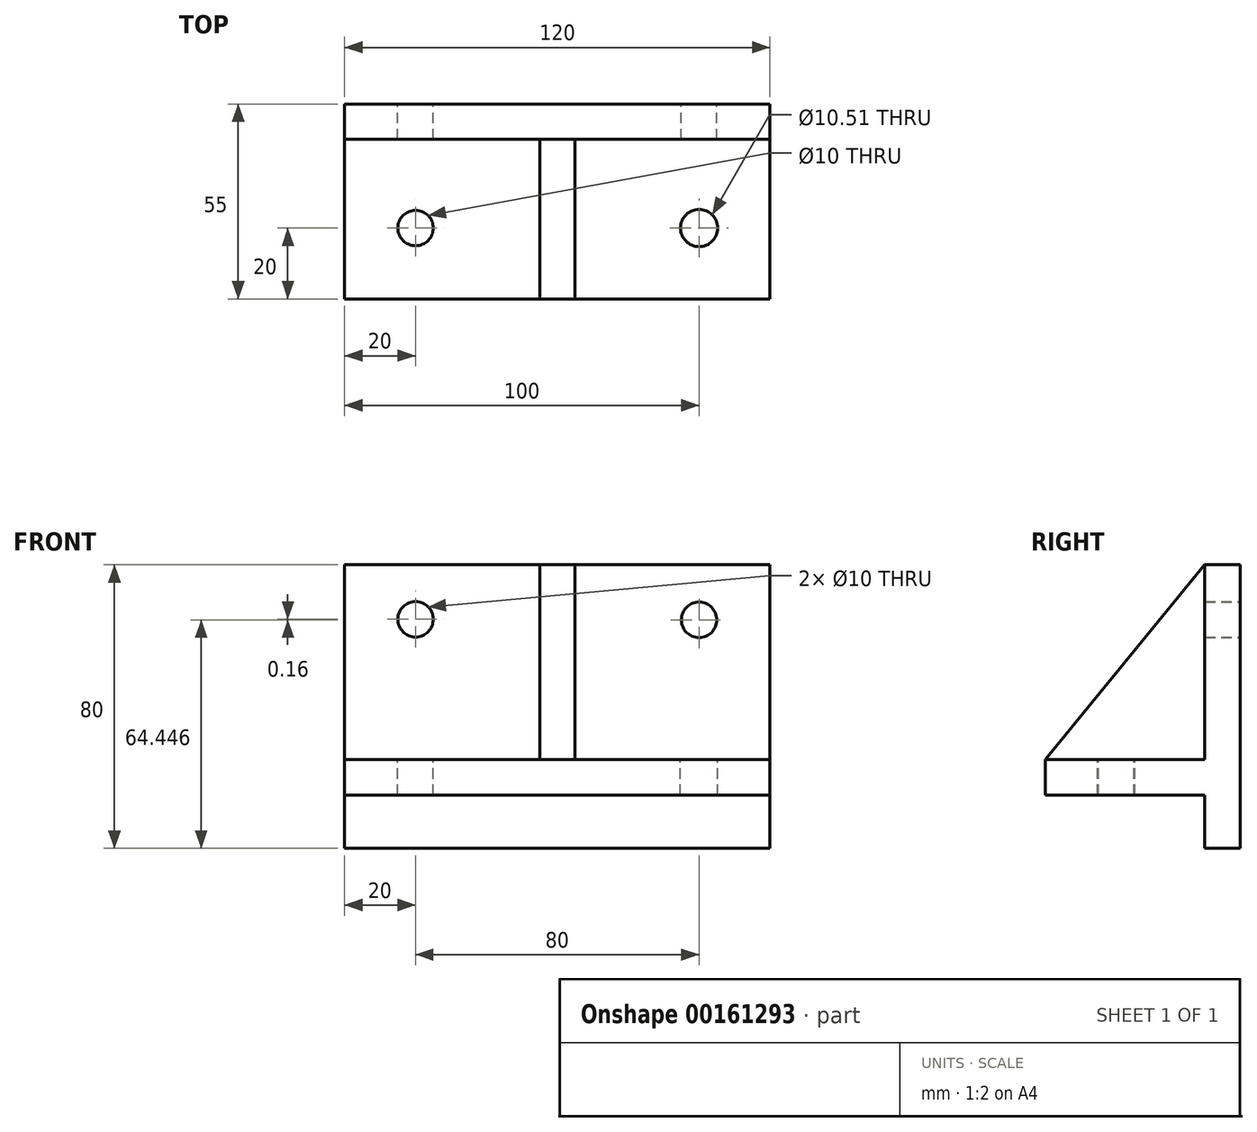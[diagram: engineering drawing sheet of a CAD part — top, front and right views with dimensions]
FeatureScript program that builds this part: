
annotation { "Feature Type Name" : "Feature", "Feature Type Description" : "" }
export const myFeature = defineFeature(function(context is Context, id is Id, definition is map)
    precondition{}
    {
        {
            var Q0;
            Q0=qCreatedBy(makeId("Front.planeOp"),FACE);
            var sketch = newSketch(context, id + "F0", { "sketchPlane" : qUnion([Q0])});
            skLineSegment(sketch, "E0.bottom", {"start": v(60, 40) * mm, "end": v(-60, 40) * mm});
            skLineSegment(sketch, "E0.top", {"start": v(60, -40) * mm, "end": v(-60, -40) * mm});
            skLineSegment(sketch, "E0.left", {"start": v(60, 40) * mm, "end": v(60, -40) * mm});
            skLineSegment(sketch, "E0.right", {"start": v(-60, 40) * mm, "end": v(-60, -40) * mm});
            skPoint(sketch, "E0.middle", {"position": v(0, 0) * mm});
            skCircle(sketch, "E1", {"center": v(-40, 24.6) * mm, "radius": 5 * mm});
            skCircle(sketch, "E2", {"center": v(40, 24.45) * mm, "radius": 5 * mm});
            skLineSegment(sketch, "E3", {"start": v(-60, 43.18) * mm, "end": v(-60, -11.82) * mm});
            skLineSegment(sketch, "E4", {"start": v(-60, -11.82) * mm, "end": v(60, -11.82) * mm});
            skLineSegment(sketch, "E5", {"start": v(-60, -11.82) * mm, "end": v(-60, -25) * mm});
            skLineSegment(sketch, "E6", {"start": v(-60, -25) * mm, "end": v(60, -25) * mm});
            skSolve(sketch);
        }
        {
            var Q0;
            {var subQ0=sQuery(id+"F0.wireOp",EDGE,"E0.top");Q0=makeQuery(id+"F0.imprint","IMPRINT",FACE,{"disambiguationData":[TD([[makeQuery(id+"F0.imprint","IMPRINT",EDGE,{"derivedFrom":subQ0}),-1.0]])]});}
            var Q1;
            {var subQ0=sQuery(id+"F0.wireOp",EDGE,"E4");Q1=makeQuery(id+"F0.imprint","IMPRINT",FACE,{"disambiguationData":[TD([[makeQuery(id+"F0.imprint","IMPRINT",EDGE,{"derivedFrom":subQ0}),-1.0]])]});}
            var Q2;
            {var subQ1=sQuery(id+"F0.wireOp",EDGE,"E0.bottom");Q2=makeQuery(id+"F0.imprint","IMPRINT",FACE,{"disambiguationData":[TD([[makeQuery(id+"F0.imprint","IMPRINT",EDGE,{"derivedFrom":subQ1}),1.0]])]});}
            extrude(context, id + "F1", {"entities" : qUnion([Q0, Q1, Q2]), "depth" : 10 * mm});
        }
        {
            var Q0;
            Q0=makeQuery(id+"F1.opExtrude","CAP_FACE",FACE,{"disambiguationData":[OSD([sQuery(id+"F0.wireOp",EDGE,"E0.bottom"),sQuery(id+"F0.wireOp",EDGE,"E0.top"),sQuery(id+"F0.wireOp",EDGE,"E0.left"),sQuery(id+"F0.wireOp",EDGE,"E0.right"),sQuery(id+"F0.wireOp",EDGE,"E1"),sQuery(id+"F0.wireOp",EDGE,"E2"),sQuery(id+"F0.wireOp",EDGE,"E3"),sQuery(id+"F0.wireOp",EDGE,"E5")])],"isStart":false});
            var sketch = newSketch(context, id + "F2", { "sketchPlane" : qUnion([Q0])});
            skLineSegment(sketch, "E7", {"start": v(-60, 40) * mm, "end": v(-60, -15) * mm});
            skLineSegment(sketch, "E8", {"start": v(-60, -15) * mm, "end": v(60, -15) * mm});
            skLineSegment(sketch, "E9", {"start": v(-60, -15) * mm, "end": v(-60, -25) * mm});
            skLineSegment(sketch, "E10", {"start": v(-60, -25) * mm, "end": v(60, -25) * mm});
            skLineSegment(sketch, "E11", {"start": v(60, -15) * mm, "end": v(60, -25) * mm});
            skSolve(sketch);
        }
        {
            var Q0;
            Q0=makeQuery(id+"F2.imprint","IMPRINT",FACE,{"disambiguationData":[TD([[makeQuery(id+"F2.imprint","IMPRINT",EDGE,{"derivedFrom":sQuery(id+"F2.wireOp",EDGE,"E8")}),-1.0]])]});
            extrude(context, id + "F3", {"entities" : qUnion([Q0]), "operationType" : NewBodyOperationType.ADD, "depth" : 45 * mm});
        }
        {
            var Q0;
            Q0=makeQuery(id+"F3.opExtrude","SWEPT_FACE",FACE,{"disambiguationData":[OSD([sQuery(id+"F2.wireOp",EDGE,"E8")])]});
            var sketch = newSketch(context, id + "F4", { "sketchPlane" : qUnion([Q0])});
            skCircle(sketch, "E12", {"center": v(-40, -35) * mm, "radius": 5 * mm});
            skCircle(sketch, "E13", {"center": v(40, -35) * mm, "radius": 5.25 * mm});
            skSolve(sketch);
        }
        {
            var Q0;
            Q0 = qSketchRegion(id + "F4", true);
            extrude(context, id + "F5", {"entities" : qUnion([Q0]), "operationType" : NewBodyOperationType.REMOVE, "oppositeDirection" : true, "depth" : 25 * mm});
        }
        {
            var Q0;
            {var subQ0=sQuery(id+"F0.wireOp",EDGE,"E1");var subQ1=sQuery(id+"F0.wireOp",EDGE,"E5");var subQ2=sQuery(id+"F0.wireOp",EDGE,"E3");var subQ3=sQuery(id+"F0.wireOp",EDGE,"E0.right");var subQ4=sQuery(id+"F0.wireOp",EDGE,"E0.left");var subQ5=sQuery(id+"F0.wireOp",EDGE,"E0.bottom");var subQ6=sQuery(id+"F0.wireOp",EDGE,"E2");Q0=makeQuery(id+"F3.boolean.opBoolean","SPLIT",FACE,{"disambiguationData":[TD([makeQuery(id+"F1.opExtrude","SWEPT_FACE",FACE,{"disambiguationData":[OSD([subQ5])]})])],"derivedFrom":makeQuery(id+"F1.opExtrude","CAP_FACE",FACE,{"disambiguationData":[OSD([subQ5,sQuery(id+"F0.wireOp",EDGE,"E0.top"),subQ4,subQ3,subQ0,subQ6,subQ2,subQ1])],"isStart":false})});}
            var sketch = newSketch(context, id + "F6", { "sketchPlane" : qUnion([Q0])});
            skLineSegment(sketch, "E14", {"start": v(-5, 40) * mm, "end": v(-5, -15) * mm});
            skLineSegment(sketch, "E15", {"start": v(5, 40) * mm, "end": v(5, -15) * mm});
            skLineSegment(sketch, "E16", {"start": v(-5, 40) * mm, "end": v(5, 40) * mm});
            skLineSegment(sketch, "E17", {"start": v(5, -15) * mm, "end": v(60, -15) * mm});
            skLineSegment(sketch, "E18", {"start": v(-5, -15) * mm, "end": v(-60, -15) * mm});
            skSolve(sketch);
        }
        {
            var Q0;
            {var subQ0=sQuery(id+"F6.wireOp",EDGE,"E14");Q0=makeQuery(id+"F6.imprint","IMPRINT",FACE,{"disambiguationData":[TD([[makeQuery(id+"F6.imprint","IMPRINT",EDGE,{"derivedFrom":subQ0}),1.0]])]});}
            extrude(context, id + "F7", {"entities" : qUnion([Q0]), "operationType" : NewBodyOperationType.ADD, "depth" : 45 * mm});
        }
        {
            var Q0;
            Q0=makeQuery(id+"F7.opExtrude","SWEPT_FACE",FACE,{"disambiguationData":[OSD([sQuery(id+"F6.wireOp",EDGE,"E15")])]});
            var sketch = newSketch(context, id + "F8", { "sketchPlane" : qUnion([Q0])});
            skLineSegment(sketch, "E19", {"start": v(-10, 40) * mm, "end": v(-55, -15) * mm});
            skLineSegment(sketch, "E20", {"start": v(-10, 40) * mm, "end": v(-55, 40) * mm});
            skLineSegment(sketch, "E21", {"start": v(-55, 40) * mm, "end": v(-55, -15) * mm});
            skSolve(sketch);
        }
        {
            var Q0;
            Q0 = qSketchRegion(id + "F8", true);
            extrude(context, id + "F9", {"entities" : qUnion([Q0]), "operationType" : NewBodyOperationType.REMOVE, "oppositeDirection" : true, "depth" : 10 * mm});
        }
    });
